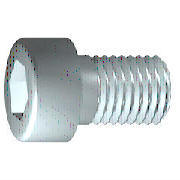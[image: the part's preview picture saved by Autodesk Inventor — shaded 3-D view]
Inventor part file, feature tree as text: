
AUTODESK INVENTOR PART (.ipt)
format: ipt  version: 2017 (Build 210142000, 142)  size: 182,784 bytes
history: native  units: mm (DEFAULTED — no unit token found)
features: sketch x2, extrude x1, plane x1, fillet x1
ambient origin geometry x7: Origin, YZ Plane, XY Plane, X Axis, Y Axis, Z Axis, Center Point
bodies: Solid1 (feature_tree), Body (feature_tree)
feature tree (5):
  extrude  "Slot"  Depth=1.5876mm
  plane  "Work Plane1"
  fillet  "Fillet2"  Radius=3.175mm
  sketch  "Sketch1"  dims[d1=19.05mm d2=1.5876mm d3=3.175mm]
  sketch  "Sketch2"  dims[d4=1.4478mm d5=60.0deg d6=3.175mm d7=3.175mm d8=2.756963mm d9=5.207mm d10=90.0deg d11=10.0mm d12=0.0mm d13=19.05mm d14=0.0mm d15=0.37846mm d16=0.37846mm d17=0.3048mm d19=0.0mm d26=38.1mm d27=45.0deg d28=0.0mm d29=0.0mm d30=0.127mm]
